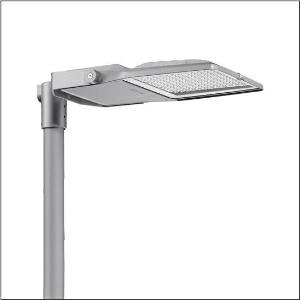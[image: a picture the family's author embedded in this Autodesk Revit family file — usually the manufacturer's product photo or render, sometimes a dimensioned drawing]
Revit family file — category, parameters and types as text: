
# Revit family: floodlight_fl_21_midi___pl61_5xa7786f2c3a_551f
name_source: partatom
category: Lighting Fixtures
units: mm (PartAtom-declared; Revit-internal decimal feet)

## family parameters
Cut with Voids When Loaded = No
Host = Face
Light Source = No
Part Type = Normal
Room Calculation Point = No
Round Connector Dimension = Use Diameter
Shared = No

## types (1)
- --- (1 x LED, 35100 lm, 271.6 W, 3000K)
    Apparent Load = 272 VA
    CIE Flux Codes = 33 65 98 100 100
    Color Rendering = 70
    Color Temperature = 3000K
    Default Elevation = 1800 mm
    Description = Floodlight FL 21 midi, floodlight, primary light control with lens, of PMMA, primary optical cover: protective disc, of toughened safety glass, transparent, light distribution: PL61, light emission: direct distribution, installation type: surface-mounted, LED, High Power LED, rated luminous flux: 35.100lm, luminous efficacy: 129lm/W, light colour: 730, colour temperature: 3000K, control gear: ECG Smart Interface, control: flexible luminous flux parameterisation, time-dependent luminous flux control, constant luminous flux control, overheat protection, pre-setting: logarithmic dimming characteristic, with terminal, 6-pole, mains connection: 220..240V, AC, 50/60Hz, start of lifetime: 272W, end of service life: 287W, reduction: 123W, luminaire housing, of diecast aluminium, powder-coated, Siteco® metallic grey (DB 702S), corrosivity category C5 mid according to DIN EN ISO 12944, sealing non-destructively replaceable, please order mast flange separately, mast bracket, of steel, galvanised, powder-coated, Siteco® metallic grey (DB 702S), Smart Interface below and above, protection rating (complete): IP66, insulation class (complete): insulation class II (safety insulation), certification: CE, ENEC, VDE, protection symbol: D, impact resistance: IK08, permissible operating ambient temperature: -40..+40°C, permissible operating ambient temperature for outdoor applications: -40..+50°C, standard: DIN EN 12944, LABS conformity tested according to VDMA 24364:2018-05, packaging unit: 1 piece

Light Distribution: PL61
    Height = 76 mm
    Lamp = 1 x LED
    Lamp Light Flux = 35100 lm
    Lamp Power = 271.6 W
    Lamp count = 1
    Length = 657 mm
    Luminous efficacy = 129 lm/W
    Manufacturer = Siteco
    ModVariant = No
    Model = 5XA7786F2C3A
    Number of Poles = 1
    OnlyDefault = Yes
    Power Factor = 1
    Product Name = Floodlight FL 21 midi | PL61
    Product group = floodlight | pylon annexe
    ProductGroupID = 6200
    Protection Class = Protection class II
    Protection Degree = IP 66
    RLX_Detail_Level = 1
    RLX_Emergency_Light_Flux = 0 lm
    RLX_Emergency_Type = 0
    RLX_Emergency_Type_DB = No
    RlxData = <blob elided: 153697 chars, md5=97da1e3d>
    Socket = socket
    Standby Power = 0 W
    System Light Flux = 35100 lm
    System Power = 272 W
    Type Comments = factory setting: luminous flux: 100 % | dim-lin: 254 | 620 mA
    Type Image = l_1007123.jpg
    URL = http://relux.com
    VarID = @adj_166609
    Voltage = 0 V
    Weight = 0.00 kg
    Width = 442 mm

## geometry (parser evidence)
native form markers: Blend x4, Sweep x13
no freeform markers — native parametric forms only
